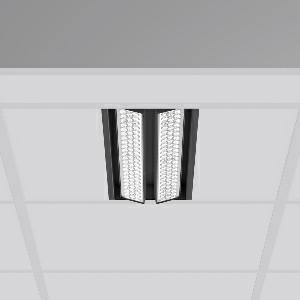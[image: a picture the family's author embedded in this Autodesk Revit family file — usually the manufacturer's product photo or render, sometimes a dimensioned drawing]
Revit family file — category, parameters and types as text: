
# Revit family: tx-move_901733_003_3_9b76
name_source: partatom
category: Lighting Fixtures
units: mm (PartAtom-declared; Revit-internal decimal feet)

## family parameters
Cut with Voids When Loaded = No
Host = Face
Light Source = No
Part Type = Normal
Room Calculation Point = No
Round Connector Dimension = Use Diameter
Shared = No

## types (1)
- MultiLumen 1 (1 x LED Modul 835, 2825 lm, 3500)
    Apparent Load = 35 VA
    CIE Flux Codes = 77 96 99 100 100
    Color Rendering = 80
    Color Temperature = 3500
    Default Elevation = 1800 mm
    Description = Series: TX-MOVE
Einlege/Einbau-Flächenstrahler. Housing: sheet steel, powder-coated. 2xSwivel range: 90°. High-efficiency LED units with optimum light control thanks to clear plastic (PC) lens optics. Spezielle Mikrostrukturen reduzieren Gelbsaum. Symmetrical light distribution. Suitable for laying in grid ceiling module 600. Connected converter included in separate gearbox.Suitable for through-wiring.MultiLumen: Luminous flux adjustable in 3 steps. Accessories: Mounting frame for installation in suspended ceilings. Environmentally friendly and resource-saving due to replaceable and recyclable components. 
Colour: deep black, matt (RAL 9005)
Length: 597 mm
Width: 190 mm
Height: 39 mm
Cut-out length: 577.5 mm
Cut-out width: 174 mm
Recess height: 100 mm
Lamp: LED
Socket: without socket
Colour temperature: 3500K
Colour rendering index (CRI): 80
System power: 35 W
Rated luminous flux: 5650 lm
Luminous efficiency: 161 lm/W
System power 2: 47 W
Rated luminous flux 2: 7350 lm
Luminous efficiency 2: 156 lm/W
System power 3: 68 W
Rated luminous flux 3: 10000 lm
Luminous efficiency 3: 147 lm/W
Control gear: Regulated power supply
Protection class: I
Type of protection: IP 20
    Height = 0 mm  [stored 0 ft]
    Lamp = 1 x LED Modul 835
    Lamp Light Flux = 2825 lm
    Lamp count = 1
    Length = 597 mm
    Lifetime = 50000 h
    Luminous efficacy = 161 lm/W
    Manufacturer = RZB
    ModVariant = No
    Model = 901733.003.3
    Mounting Place = Ceiling, Wall
    Mounting Type = Recessed
    Number of Poles = 1
    OnlyDefault = Yes
    Power Factor = 1
    Product Name = TX-MOVE
    Product group = Recessed projectors
    ProductGroupID = 401
    Protection Class = Protection class I
    Protection Degree = IP 20
    RLX_Detail_Level = 1
    RLX_Emergency_Light_Flux = 0 lm
    RLX_Emergency_Type = 0
    RLX_Emergency_Type_DB = No
    RlxData = <blob elided: 36909 chars, md5=c756576a>
    Socket = socket
    Standby Power = 0 W
    System Light Flux = 5650 lm
    System Power = 35 W
    Type Comments = MultiLumen 1
    Type Image = 901733.003.jpg
    URL = http://relux.com
    VarID = multilumen_1
    Voltage = 230 V
    Voltage Range = 220-240 V
    Weight = 0.00 kg
    Width = 190 mm  [stored 0.62336 ft]

note: [stored X ft] marks values corroborated as IEEE doubles in the binary element streams (Revit-internal decimal feet)

## geometry (parser evidence)
native form markers: Blend x4, Sweep x12
no freeform markers — native parametric forms only
